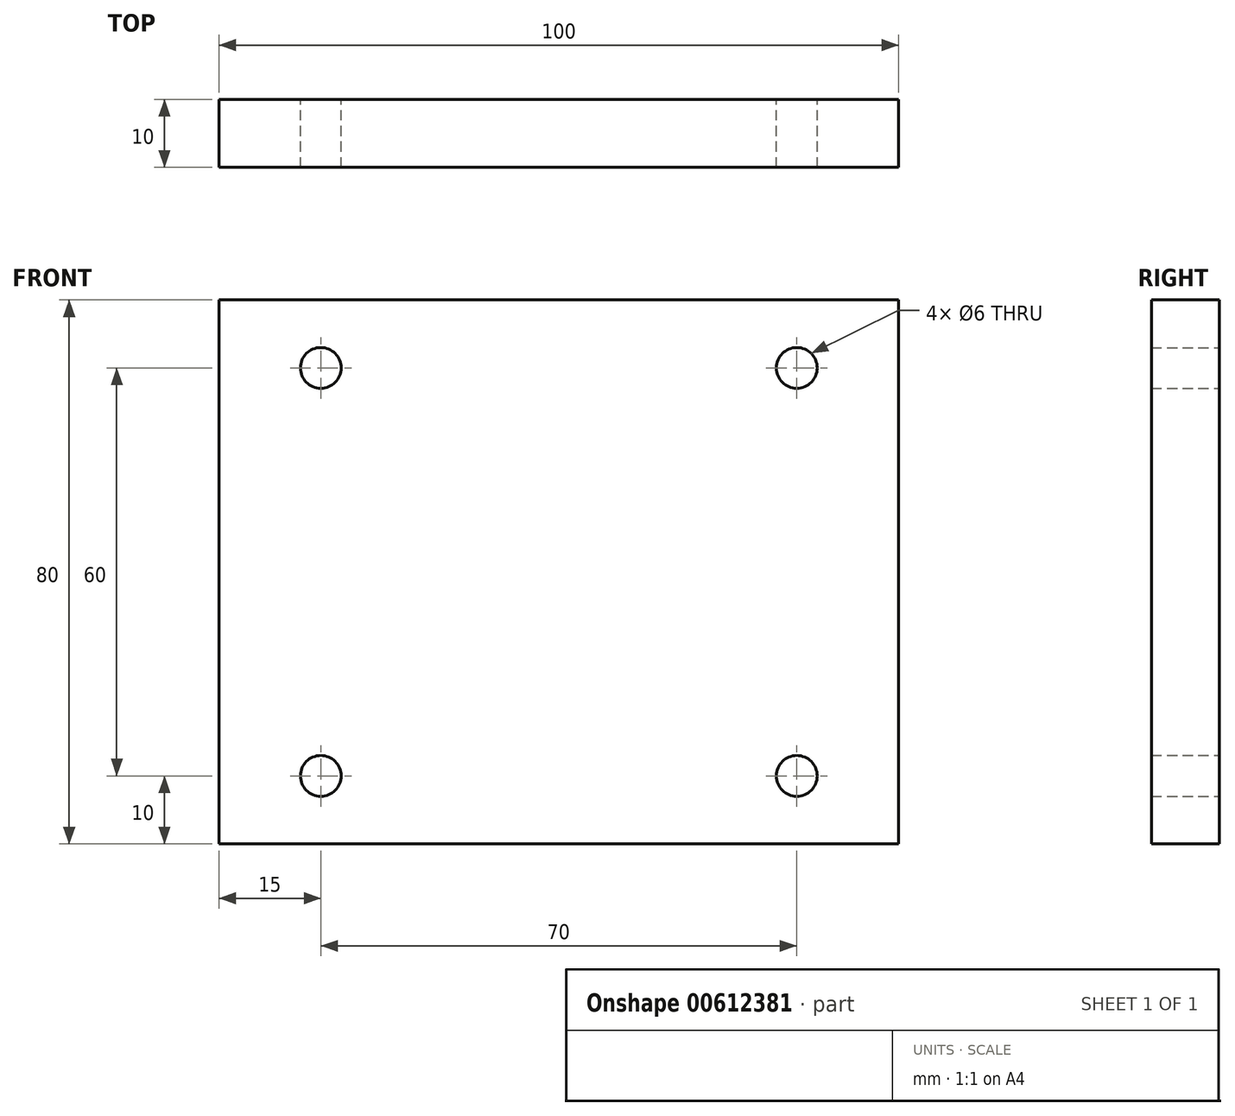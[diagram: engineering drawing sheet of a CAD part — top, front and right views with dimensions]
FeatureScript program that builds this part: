
annotation { "Feature Type Name" : "Feature", "Feature Type Description" : "" }
export const myFeature = defineFeature(function(context is Context, id is Id, definition is map)
    precondition{}
    {
        {
            var Q0;
            Q0=qCreatedBy(makeId("Front.planeOp"),FACE);
            var sketch = newSketch(context, id + "F0", { "sketchPlane" : qUnion([Q0])});
            skLineSegment(sketch, "E0.bottom", {"start": v(0, 0) * mm, "end": v(100, 0) * mm});
            skLineSegment(sketch, "E0.top", {"start": v(0, 80) * mm, "end": v(100, 80) * mm});
            skLineSegment(sketch, "E0.left", {"start": v(0, 0) * mm, "end": v(0, 80) * mm});
            skLineSegment(sketch, "E0.right", {"start": v(100, 0) * mm, "end": v(100, 80) * mm});
            skCircle(sketch, "E1", {"center": v(15, 70) * mm, "radius": 3 * mm});
            skCircle(sketch, "E2", {"center": v(85, 70) * mm, "radius": 3 * mm});
            skCircle(sketch, "E3", {"center": v(85, 10) * mm, "radius": 3 * mm});
            skCircle(sketch, "E4", {"center": v(15, 10) * mm, "radius": 3 * mm});
            skSolve(sketch);
        }
        {
            var Q0;
            Q0=makeQuery(id+"F0.imprint","IMPRINT",FACE,{"disambiguationData":[TD([[makeQuery(id+"F0.imprint","IMPRINT",EDGE,{"derivedFrom":sQuery(id+"F0.wireOp",EDGE,"E0.bottom")}),1.0]])]});
            extrude(context, id + "F1", {"entities" : qUnion([Q0]), "depth" : 10 * mm, "offsetDistance" : 25 * mm});
        }
    });
